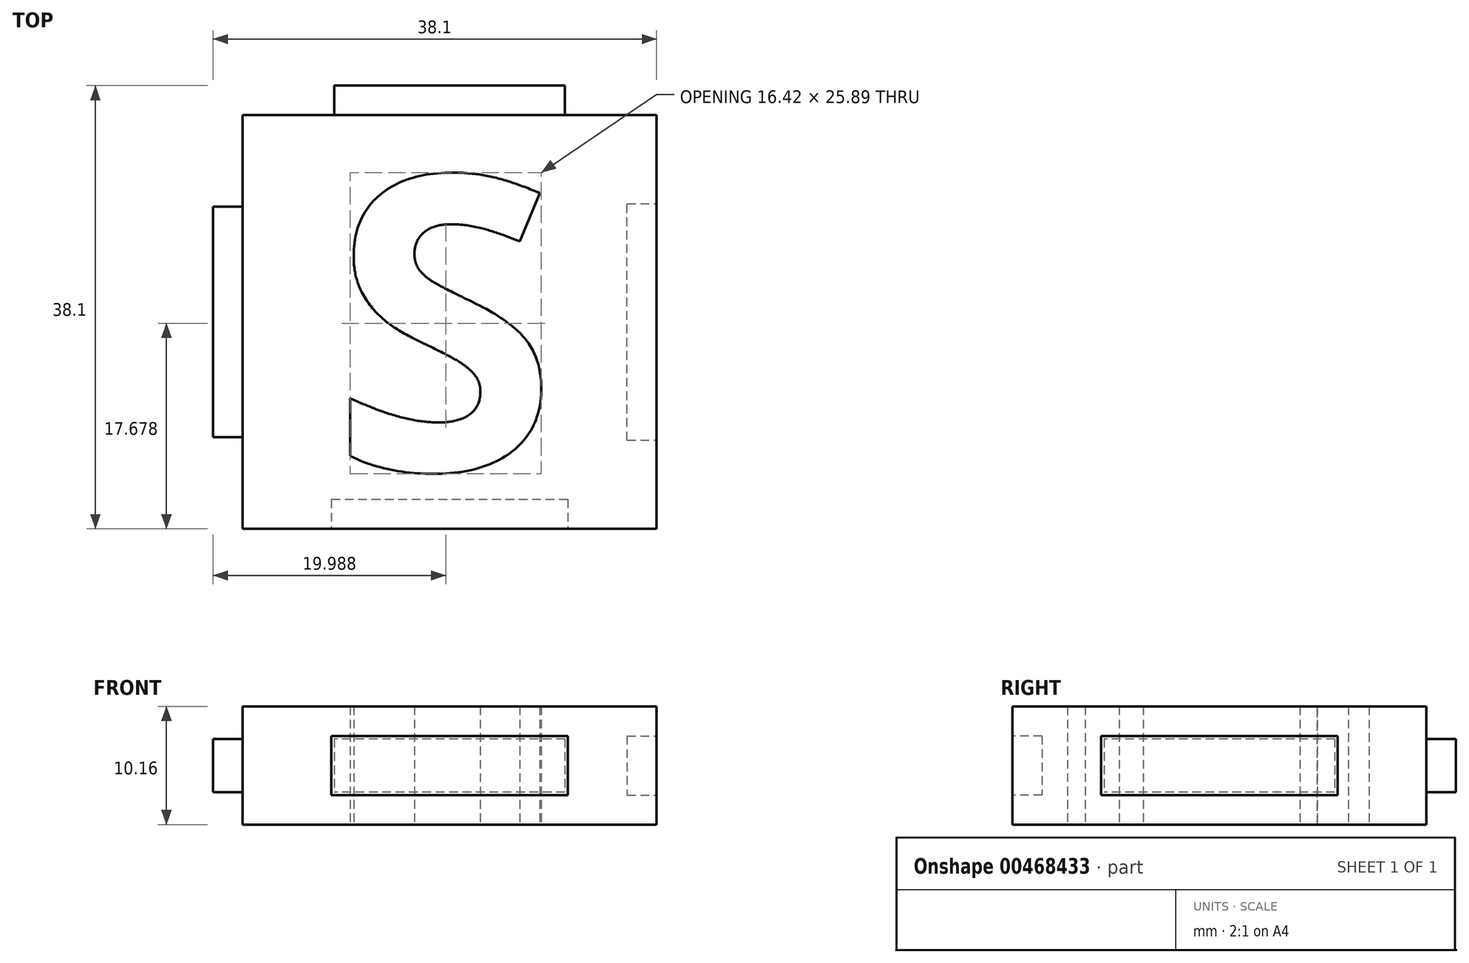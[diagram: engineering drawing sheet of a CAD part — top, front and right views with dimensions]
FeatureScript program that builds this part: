
annotation { "Feature Type Name" : "Feature", "Feature Type Description" : "" }
export const myFeature = defineFeature(function(context is Context, id is Id, definition is map)
    precondition{}
    {
        {
            var Q0;
            Q0=qCreatedBy(makeId("Top.planeOp"),FACE);
            var sketch = newSketch(context, id + "F0", { "sketchPlane" : qUnion([Q0])});
            skLineSegment(sketch, "E0.bottom", {"start": v(-17.78, 17.78) * mm, "end": v(17.78, 17.78) * mm});
            skLineSegment(sketch, "E0.top", {"start": v(-17.78, -17.78) * mm, "end": v(17.78, -17.78) * mm});
            skLineSegment(sketch, "E0.left", {"start": v(-17.78, 17.78) * mm, "end": v(-17.78, -17.78) * mm});
            skLineSegment(sketch, "E0.right", {"start": v(17.78, 17.78) * mm, "end": v(17.78, -17.78) * mm});
            skText(sketch, "E1", { "text": "S", "fontName": "OpenSans-Bold.ttf"});
            const initialGuessF0  = {"E1": [-0.01016, -0.0127, 1, 0, 0.0254]};
            skSetInitialGuess(sketch, initialGuessF0);
            skSolve(sketch);
        }
        {
            var Q0;
            Q0=qSketchRegion(id+"F0",true);
            extrude(context, id + "F1", {"entities" : qUnion([Q0]), "endBound" : BoundingType.SYMMETRIC, "depth" : 10.16 * mm});
        }
        {
            var Q0;
            Q0=makeQuery(id+"F1.opExtrude","SWEPT_FACE",FACE,{"disambiguationData":[OSD([sQuery(id+"F0.wireOp",EDGE,"E0.bottom")])]});
            var sketch = newSketch(context, id + "F2", { "sketchPlane" : qUnion([Q0])});
            skLineSegment(sketch, "E2.bottom", {"start": v(-9.9, 2.29) * mm, "end": v(9.9, 2.29) * mm});
            skLineSegment(sketch, "E2.top", {"start": v(-9.9, -2.29) * mm, "end": v(9.9, -2.29) * mm});
            skLineSegment(sketch, "E2.left", {"start": v(-9.9, 2.29) * mm, "end": v(-9.9, -2.29) * mm});
            skLineSegment(sketch, "E2.right", {"start": v(9.9, 2.29) * mm, "end": v(9.9, -2.29) * mm});
            skSolve(sketch);
        }
        {
            var Q0;
            Q0=qSketchRegion(id+"F2",true);
            extrude(context, id + "F3", {"entities" : qUnion([Q0]), "operationType" : NewBodyOperationType.ADD, "depth" : 2.54 * mm});
        }
        {
            var Q0;
            Q0=makeQuery(id+"F1.opExtrude","SWEPT_FACE",FACE,{"disambiguationData":[OSD([sQuery(id+"F0.wireOp",EDGE,"E0.left")])]});
            var sketch = newSketch(context, id + "F4", { "sketchPlane" : qUnion([Q0])});
            skLineSegment(sketch, "E3.bottom", {"start": v(-9.9, 2.29) * mm, "end": v(9.9, 2.29) * mm});
            skLineSegment(sketch, "E3.top", {"start": v(-9.9, -2.29) * mm, "end": v(9.9, -2.29) * mm});
            skLineSegment(sketch, "E3.left", {"start": v(-9.9, 2.29) * mm, "end": v(-9.9, -2.29) * mm});
            skLineSegment(sketch, "E3.right", {"start": v(9.9, 2.29) * mm, "end": v(9.9, -2.29) * mm});
            skSolve(sketch);
        }
        {
            var Q0;
            Q0=qSketchRegion(id+"F4",true);
            extrude(context, id + "F5", {"entities" : qUnion([Q0]), "operationType" : NewBodyOperationType.ADD, "depth" : 2.54 * mm});
        }
        {
            var Q0;
            Q0=makeQuery(id+"F1.opExtrude","SWEPT_FACE",FACE,{"disambiguationData":[OSD([sQuery(id+"F0.wireOp",EDGE,"E0.top")])]});
            var sketch = newSketch(context, id + "F6", { "sketchPlane" : qUnion([Q0])});
            skLineSegment(sketch, "E4.bottom", {"start": v(-10.16, 2.54) * mm, "end": v(10.16, 2.54) * mm});
            skLineSegment(sketch, "E4.top", {"start": v(-10.16, -2.54) * mm, "end": v(10.16, -2.54) * mm});
            skLineSegment(sketch, "E4.left", {"start": v(-10.16, 2.54) * mm, "end": v(-10.16, -2.54) * mm});
            skLineSegment(sketch, "E4.right", {"start": v(10.16, 2.54) * mm, "end": v(10.16, -2.54) * mm});
            skSolve(sketch);
        }
        {
            var Q0;
            Q0=qSketchRegion(id+"F6",true);
            extrude(context, id + "F7", {"entities" : qUnion([Q0]), "operationType" : NewBodyOperationType.REMOVE, "oppositeDirection" : true, "depth" : 2.54 * mm});
        }
        {
            var Q0;
            Q0=makeQuery(id+"F1.opExtrude","SWEPT_FACE",FACE,{"disambiguationData":[OSD([sQuery(id+"F0.wireOp",EDGE,"E0.right")])]});
            var sketch = newSketch(context, id + "F8", { "sketchPlane" : qUnion([Q0])});
            skLineSegment(sketch, "E5.bottom", {"start": v(-10.16, 2.54) * mm, "end": v(10.16, 2.54) * mm});
            skLineSegment(sketch, "E5.top", {"start": v(-10.16, -2.54) * mm, "end": v(10.16, -2.54) * mm});
            skLineSegment(sketch, "E5.left", {"start": v(-10.16, 2.54) * mm, "end": v(-10.16, -2.54) * mm});
            skLineSegment(sketch, "E5.right", {"start": v(10.16, 2.54) * mm, "end": v(10.16, -2.54) * mm});
            skSolve(sketch);
        }
        {
            var Q0;
            Q0=qSketchRegion(id+"F8",true);
            extrude(context, id + "F9", {"entities" : qUnion([Q0]), "operationType" : NewBodyOperationType.REMOVE, "oppositeDirection" : true, "depth" : 2.54 * mm});
        }
    });
